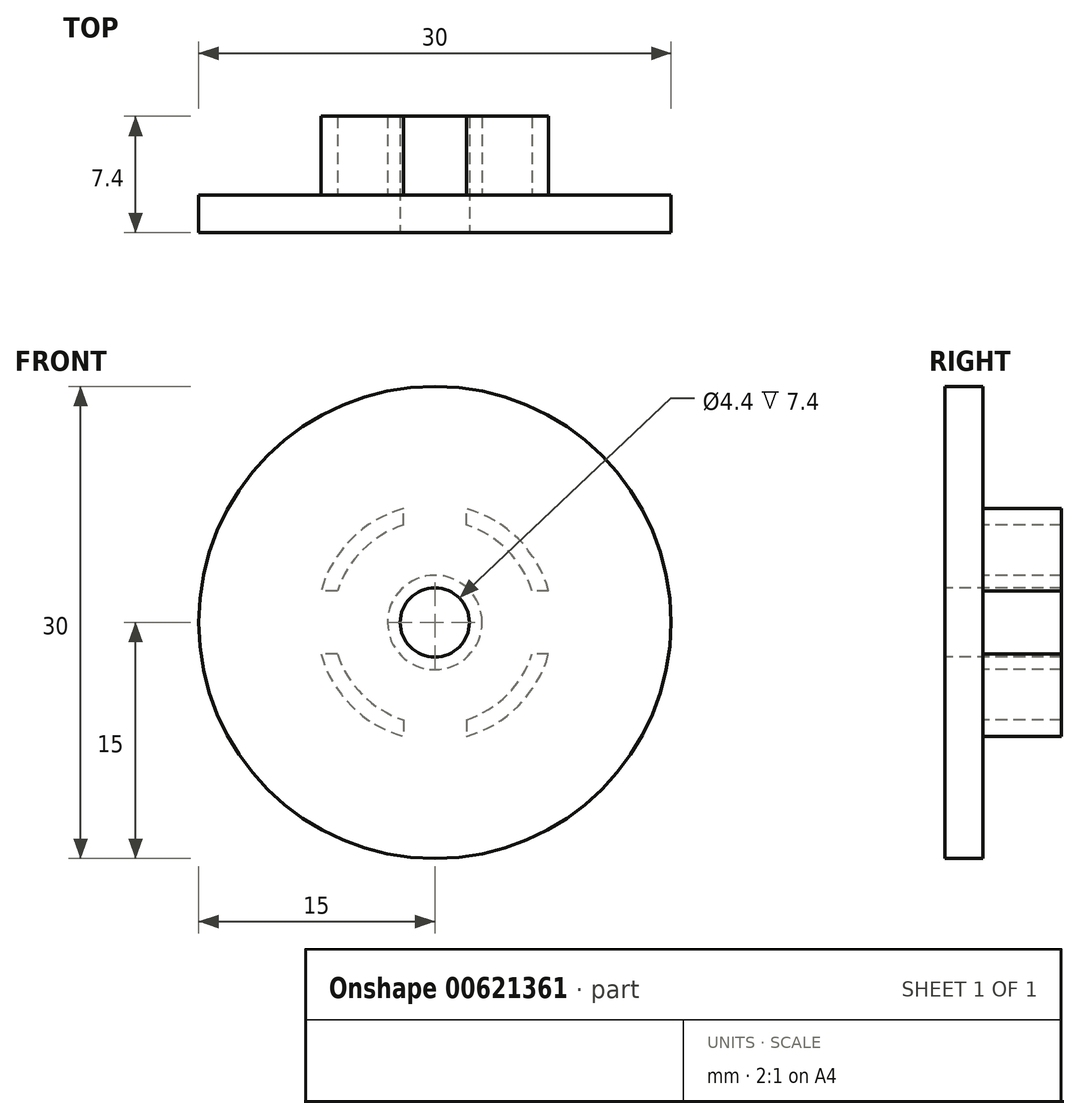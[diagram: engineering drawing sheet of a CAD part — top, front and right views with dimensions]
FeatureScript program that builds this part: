
annotation { "Feature Type Name" : "Feature", "Feature Type Description" : "" }
export const myFeature = defineFeature(function(context is Context, id is Id, definition is map)
    precondition{}
    {
        {
            var Q0;
            Q0=qCreatedBy(makeId("Front.planeOp"),FACE);
            var sketch = newSketch(context, id + "F0", { "sketchPlane" : qUnion([Q0])});
            skCircle(sketch, "E0", {"center": v(0, 0) * mm, "radius": 15 * mm});
            skSolve(sketch);
        }
        {
            var Q0;
            Q0=makeQuery(id+"F0.imprint","IMPRINT",FACE,{"disambiguationData":[TD([[makeQuery(id+"F0.imprint","IMPRINT",EDGE,{"derivedFrom":sQuery(id+"F0.wireOp",EDGE,"E0")}),1.0]])]});
            extrude(context, id + "F1", {"entities" : qUnion([Q0]), "depth" : 2.4 * mm, "offsetDistance" : 25 * mm});
        }
        {
            var Q0;
            Q0=makeQuery(id+"F1.opExtrude","CAP_FACE",FACE,{"disambiguationData":[OSD([sQuery(id+"F0.wireOp",EDGE,"E0")])],"isStart":false});
            var sketch = newSketch(context, id + "F2", { "sketchPlane" : qUnion([Q0])});
            skCircle(sketch, "E1", {"center": v(0, 0) * mm, "radius": 2.2 * mm});
            skSolve(sketch);
        }
        {
            var Q0;
            Q0=makeQuery(id+"F2.imprint","IMPRINT",FACE,{"disambiguationData":[TD([[makeQuery(id+"F2.imprint","IMPRINT",EDGE,{"derivedFrom":sQuery(id+"F2.wireOp",EDGE,"E1")}),1.0]])]});
            extrude(context, id + "F3", {"entities" : qUnion([Q0]), "operationType" : NewBodyOperationType.REMOVE, "endBound" : BoundingType.THROUGH_ALL, "oppositeDirection" : true, "depth" : 25 * mm, "offsetDistance" : 25 * mm});
        }
        {
            var Q0;
            Q0=makeQuery(id+"F1.opExtrude","CAP_FACE",FACE,{"disambiguationData":[OSD([sQuery(id+"F0.wireOp",EDGE,"E0")])],"isStart":true});
            var sketch = newSketch(context, id + "F4", { "sketchPlane" : qUnion([Q0])});
            skCircle(sketch, "E2", {"center": v(0, 0) * mm, "radius": 3 * mm});
            skArc(sketch, "E3", {"start": v(2, -6.18) * mm, "mid": v(4.6, -4.6) * mm, "end": v(6.18, -2) * mm});
            skArc(sketch, "E4", {"start": v(2, -7.23) * mm, "mid": v(5.3, -5.3) * mm, "end": v(7.23, -2) * mm});
            skLineSegment(sketch, "E5", {"start": v(-2, -6.18) * mm, "end": v(-2, -7.23) * mm});
            skLineSegment(sketch, "E6.MirrorCS", {"start": v(2, -6.18) * mm, "end": v(2, -7.23) * mm});
            skLineSegment(sketch, "E7", {"start": v(-7.23, -2) * mm, "end": v(-6.18, -2) * mm});
            skLineSegment(sketch, "E8.MirrorCS", {"start": v(-7.23, 2) * mm, "end": v(-6.18, 2) * mm});
            skLineSegment(sketch, "E9", {"start": v(-2, 6.18) * mm, "end": v(-2, 7.23) * mm});
            skLineSegment(sketch, "E10.MirrorCS", {"start": v(2, 6.18) * mm, "end": v(2, 7.23) * mm});
            skLineSegment(sketch, "E11", {"start": v(6.18, 2) * mm, "end": v(7.23, 2) * mm});
            skLineSegment(sketch, "E12.MirrorCS", {"start": v(6.18, -2) * mm, "end": v(7.23, -2) * mm});
            skArc(sketch, "E13.trimOffspring", {"start": v(6.18, 2) * mm, "mid": v(4.6, 4.6) * mm, "end": v(2, 6.18) * mm});
            skArc(sketch, "E14.trimOffspring", {"start": v(7.23, 2) * mm, "mid": v(5.3, 5.3) * mm, "end": v(2, 7.23) * mm});
            skArc(sketch, "E15.trimOffspring", {"start": v(-2, 6.18) * mm, "mid": v(-4.6, 4.6) * mm, "end": v(-6.18, 2) * mm});
            skArc(sketch, "E16.trimOffspring", {"start": v(-2, 7.23) * mm, "mid": v(-5.3, 5.3) * mm, "end": v(-7.23, 2) * mm});
            skArc(sketch, "E17.trimOffspring", {"start": v(-6.18, -2) * mm, "mid": v(-4.6, -4.6) * mm, "end": v(-2, -6.18) * mm});
            skArc(sketch, "E18.trimOffspring", {"start": v(-7.23, -2) * mm, "mid": v(-5.3, -5.3) * mm, "end": v(-2, -7.23) * mm});
            skSolve(sketch);
        }
        {
            var Q0;
            Q0=makeQuery(id+"F4.imprint","IMPRINT",FACE,{"disambiguationData":[TD([[makeQuery(id+"F4.imprint","IMPRINT",EDGE,{"derivedFrom":sQuery(id+"F4.wireOp",EDGE,"E2")}),1.0]])]});
            var Q1;
            Q1=makeQuery(id+"F4.imprint","IMPRINT",FACE,{"disambiguationData":[TD([[makeQuery(id+"F4.imprint","IMPRINT",EDGE,{"derivedFrom":sQuery(id+"F4.wireOp",EDGE,"E8.MirrorCS")}),1.0]])]});
            var Q2;
            Q2=makeQuery(id+"F4.imprint","IMPRINT",FACE,{"disambiguationData":[TD([[makeQuery(id+"F4.imprint","IMPRINT",EDGE,{"derivedFrom":sQuery(id+"F4.wireOp",EDGE,"E5")}),-1.0]])]});
            var Q3;
            Q3=makeQuery(id+"F4.imprint","IMPRINT",FACE,{"disambiguationData":[TD([[makeQuery(id+"F4.imprint","IMPRINT",EDGE,{"derivedFrom":sQuery(id+"F4.wireOp",EDGE,"E10.MirrorCS")}),-1.0]])]});
            var Q4;
            Q4=makeQuery(id+"F4.imprint","IMPRINT",FACE,{"disambiguationData":[TD([[makeQuery(id+"F4.imprint","IMPRINT",EDGE,{"derivedFrom":sQuery(id+"F4.wireOp",EDGE,"E3")}),-1.0]])]});
            extrude(context, id + "F5", {"entities" : qUnion([Q0, Q1, Q2, Q3, Q4]), "operationType" : NewBodyOperationType.ADD, "depth" : 5 * mm, "offsetDistance" : 25 * mm});
        }
    });
